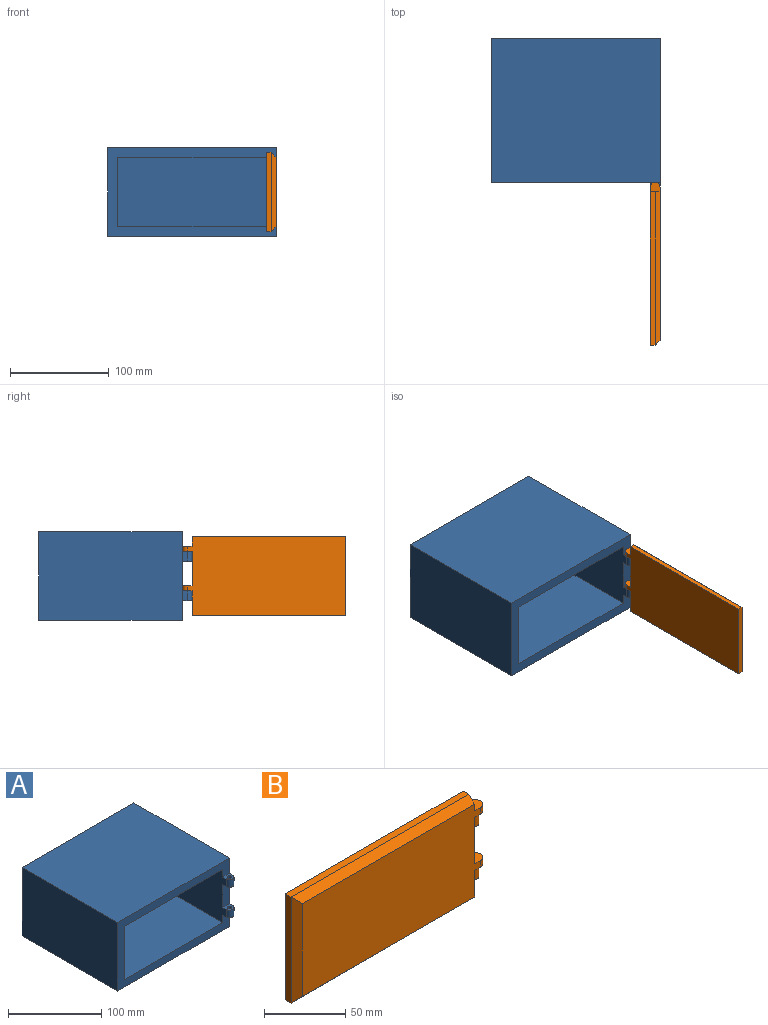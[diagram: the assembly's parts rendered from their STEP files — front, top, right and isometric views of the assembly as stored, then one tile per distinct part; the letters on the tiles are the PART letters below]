
ASSEMBLY  parts=2 mates=1
PART A: 20 faces, bbox 170x155x90 mm
  f0: plane 30x10mm, normal (0,-1,0), area 300mm2, adj f4,f9,f12,f15
  f1: plane 150x135mm, normal (0,0,1), area 20250mm2, adj f3,f7,f8,f9
  f2: plane 145x90mm, normal (-1,0,0), area 13050mm2, adj f3,f5,f6,f11
  f3: plane 170x90mm, normal (0,-1,0), area 4300mm2, adj f1,f2,f4,f6,f7,f9,f10,f11
  f4: plane 150x90mm, normal (1,0,0), area 13150mm2, adj f0,f3,f5,f6,f11,f12,f13,f14
  f5: plane 170x90mm, normal (0,1,0), area 15300mm2, adj f2,f4,f6,f11
  f6: plane 170x145mm, normal (0,0,-1), area 24650mm2, adj f2,f3,f4,f5
  f7: plane 135x70mm, normal (1,0,0), area 9450mm2, adj f1,f3,f8,f10
  f8: plane 150x70mm, normal (0,-1,0), area 10500mm2, adj f1,f7,f9,f10
  f9: plane 140x70mm, normal (-1,0,0), area 9550mm2, adj f0,f1,f3,f8,f10,f12,f13,f14
  f10: plane 150x135mm, normal (0,0,-1), area 20250mm2, adj f3,f7,f8,f9
  f11: plane 170x145mm, normal (0,0,1), area 24650mm2, adj f2,f3,f4,f5
  f12: plane 10x10mm, normal (0,0,1), area 69.6mm2, adj f0,f4,f9,f17,f19
  f13: plane 10x10mm, normal (0,0,-1), area 69.6mm2, adj f3,f4,f9,f17,f19
  f14: plane 10x10mm, normal (0,0,1), area 69.6mm2, adj f3,f4,f9,f16,f18
  f15: plane 10x10mm, normal (0,0,-1), area 69.6mm2, adj f0,f4,f9,f16,f18
  f16: cylinder r=5mm len=10mm, axis (0,0,-1), area 157.1mm2, adj f4,f9,f14,f15
  f17: cylinder r=5mm len=10mm, axis (0,0,-1), area 157.1mm2, adj f4,f9,f12,f13
  f18: cylinder r=2.5mm len=10mm, axis (0,0,1), area 157.1mm2, adj f14,f15
  f19: cylinder r=2.5mm len=10mm, axis (0,0,1), area 157.1mm2, adj f12,f13
PART B: 21 faces, bbox 165x10x80 mm
  f0: plane 25x10mm, normal (1,0,0), area 237.5mm2, adj f5,f6,f7,f10,f15
  f1: plane 35x10mm, normal (1,0,0), area 350mm2, adj f6,f7,f12,f14
  f2: plane 10x10mm, normal (1,0,0), area 87.5mm2, adj f3,f6,f7,f8,f11
  f3: plane 155x5mm, normal (0,0,1), area 775mm2, adj f2,f4,f7,f8
  f4: plane 80x5mm, normal (-1,0,0), area 400mm2, adj f3,f5,f7,f9
  f5: plane 155x5mm, normal (0,0,-1), area 775mm2, adj f0,f4,f7,f10
  f6: plane 155x70mm, normal (0,-1,0), area 10550mm2, adj f0,f1,f2,f8,f9,f10,f11,f12
  f7: plane 160x80mm, normal (0,1,0), area 12450mm2, adj f0,f1,f2,f3,f4,f5,f11,f12
  f8: plane 155x5mm, normal (0,-0.71,0.71), area 1078.3mm2, adj f2,f3,f6,f9
  f9: plane 80x5mm, normal (-0.71,-0.71,0), area 530.3mm2, adj f4,f6,f8,f10
  f10: plane 155x5mm, normal (0,-0.71,-0.71), area 1078.3mm2, adj f0,f5,f6,f9
  f11: plane 10x10mm, normal (0,0,1), area 89.3mm2, adj f2,f6,f7,f13
  f12: plane 10x10mm, normal (0,0,-1), area 69.6mm2, adj f1,f6,f7,f13,f17
  f13: cylinder r=5mm len=10mm, axis (0,0,1), area 78.5mm2, adj f6,f7,f11,f12
  f14: plane 10x10mm, normal (0,0,1), area 89.3mm2, adj f1,f6,f7,f16
  f15: plane 10x10mm, normal (0,0,-1), area 69.6mm2, adj f0,f6,f7,f16,f19
  f16: cylinder r=5mm len=10mm, axis (0,0,1), area 78.5mm2, adj f6,f7,f14,f15
  f17: cylinder r=2.5mm len=10mm, axis (0,0,1), area 157.1mm2, adj f12,f18
  f18: plane 5x5mm, normal (0,0,-1), area 19.6mm2, adj f17
  f19: cylinder r=2.5mm len=10mm, axis (0,0,1), area 157.1mm2, adj f15,f20
  f20: plane 5x5mm, normal (0,0,-1), area 19.6mm2, adj f19
PLACE A t=(-4.64,47.48,-26.46)mm
PLACE B rot(axis=(0,0,1),90deg) t=(-7.14,-115.02,-26.46)mm
MATE revolute B.f13 <-> A.f16  axis (0,0,-1) through (75.36,-35.02,43.54)mm
